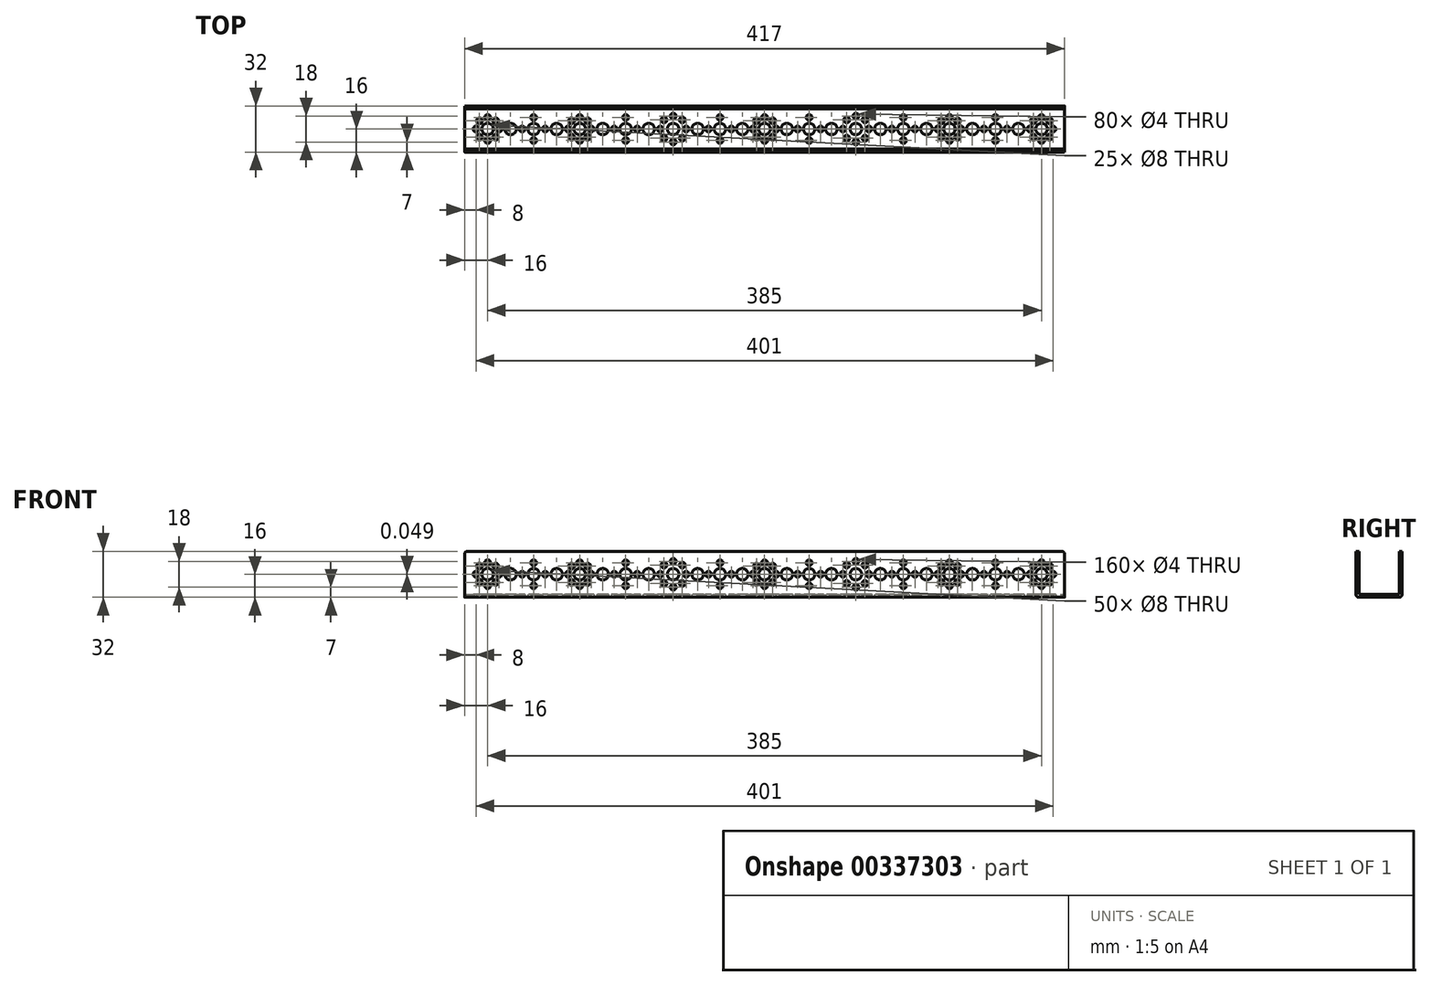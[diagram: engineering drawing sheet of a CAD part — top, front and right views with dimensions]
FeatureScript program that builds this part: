
annotation { "Feature Type Name" : "Feature", "Feature Type Description" : "" }
export const myFeature = defineFeature(function(context is Context, id is Id, definition is map)
    precondition{}
    {
        {
            var Q0;
            Q0=qCreatedBy(makeId("Top.planeOp"),FACE);
            var sketch = newSketch(context, id + "F0", { "sketchPlane" : qUnion([Q0])});
            skLineSegment(sketch, "E0", {"start": v(-32.28, 88.8) * mm, "end": v(-32.28, 86.16) * mm});
            skLineSegment(sketch, "E1", {"start": v(-32.28, 86.16) * mm, "end": v(-32.28, 83.52) * mm});
            skLineSegment(sketch, "E2", {"start": v(-34.35, 86.16) * mm, "end": v(-32.28, 86.16) * mm});
            skLineSegment(sketch, "E3", {"start": v(-30.23, 86.16) * mm, "end": v(-32.28, 86.16) * mm});
            skLineSegment(sketch, "E4", {"start": v(-32.28, 86.16) * mm, "end": v(-30.85, 87.6) * mm});
            skLineSegment(sketch, "E5", {"start": v(-32.28, 86.16) * mm, "end": v(-33.68, 84.77) * mm});
            skLineSegment(sketch, "E6", {"start": v(-32.28, 86.16) * mm, "end": v(-33.68, 87.56) * mm});
            skLineSegment(sketch, "E7", {"start": v(-32.28, 86.16) * mm, "end": v(-30.63, 84.51) * mm});
            skCircle(sketch, "E8", {"center": v(-32.28, 86.16) * mm, "radius": 4 * mm});
            skCircle(sketch, "E9", {"center": v(-38.65, 92.53) * mm, "radius": 2 * mm});
            skCircle(sketch, "E10", {"center": v(-32.28, 95.16) * mm, "radius": 2 * mm});
            skCircle(sketch, "E11", {"center": v(-25.92, 92.53) * mm, "radius": 2 * mm});
            skCircle(sketch, "E12", {"center": v(-23.28, 86.16) * mm, "radius": 2 * mm});
            skCircle(sketch, "E13", {"center": v(-41.28, 86.16) * mm, "radius": 2 * mm});
            skCircle(sketch, "E14", {"center": v(-38.65, 79.8) * mm, "radius": 2 * mm});
            skCircle(sketch, "E15", {"center": v(-32.28, 77.16) * mm, "radius": 2 * mm});
            skCircle(sketch, "E16", {"center": v(-25.92, 79.8) * mm, "radius": 2 * mm});
            skCircle(sketch, "E17", {"center": v(-14.28, 86.16) * mm, "radius": 4 * mm});
            skCircle(sketch, "E18", {"center": v(3.72, 86.16) * mm, "radius": 4 * mm});
            skCircle(sketch, "E19", {"center": v(3.72, 95.16) * mm, "radius": 2 * mm});
            skCircle(sketch, "E20", {"center": v(12.72, 86.16) * mm, "radius": 2 * mm});
            skCircle(sketch, "E21", {"center": v(3.72, 77.16) * mm, "radius": 2 * mm});
            skCircle(sketch, "E22", {"center": v(-5.28, 86.16) * mm, "radius": 2 * mm});
            skCircle(sketch, "E23", {"center": v(21.72, 86.16) * mm, "radius": 4 * mm});
            skLineSegment(sketch, "E24.bottom", {"start": v(208.5, 16) * mm, "end": v(-208.5, 16) * mm});
            skLineSegment(sketch, "E24.top", {"start": v(208.5, -16) * mm, "end": v(-208.5, -16) * mm});
            skLineSegment(sketch, "E24.left", {"start": v(208.5, 16) * mm, "end": v(208.5, -16) * mm});
            skLineSegment(sketch, "E24.right", {"start": v(-208.5, 16) * mm, "end": v(-208.5, -16) * mm});
            skPoint(sketch, "E24.middle", {"position": v(0, 0) * mm});
            skLineSegment(sketch, "E25", {"start": v(-192.5, 2.64) * mm, "end": v(-192.5, 0) * mm});
            skLineSegment(sketch, "E26", {"start": v(-192.5, 0) * mm, "end": v(-192.5, -2.64) * mm});
            skLineSegment(sketch, "E27", {"start": v(-194.35, 0) * mm, "end": v(-192.5, 0) * mm});
            skLineSegment(sketch, "E28", {"start": v(-188.78, 0) * mm, "end": v(-192.5, 0) * mm});
            skLineSegment(sketch, "E29", {"start": v(-192.5, 0) * mm, "end": v(-191.22, 1.28) * mm});
            skLineSegment(sketch, "E30", {"start": v(-192.5, 0) * mm, "end": v(-193.9, -1.4) * mm});
            skLineSegment(sketch, "E31", {"start": v(-192.5, 0) * mm, "end": v(-193.9, 1.4) * mm});
            skLineSegment(sketch, "E32", {"start": v(-192.5, 0) * mm, "end": v(-191.12, -1.38) * mm});
            skCircle(sketch, "E33", {"center": v(-192.5, 0) * mm, "radius": 4 * mm});
            skCircle(sketch, "E34", {"center": v(-198.16, 5.66) * mm, "radius": 2 * mm});
            skCircle(sketch, "E35", {"center": v(-192.5, 8) * mm, "radius": 2 * mm});
            skCircle(sketch, "E36", {"center": v(-186.84, 5.66) * mm, "radius": 2 * mm});
            skCircle(sketch, "E37", {"center": v(-184.5, 0) * mm, "radius": 2 * mm});
            skCircle(sketch, "E38", {"center": v(-200.5, 0) * mm, "radius": 2 * mm});
            skCircle(sketch, "E39", {"center": v(-198.16, -5.66) * mm, "radius": 2 * mm});
            skCircle(sketch, "E40", {"center": v(-192.5, -8) * mm, "radius": 2 * mm});
            skCircle(sketch, "E41", {"center": v(-186.84, -5.66) * mm, "radius": 2 * mm});
            skCircle(sketch, "E42", {"center": v(-176.5, 0) * mm, "radius": 4 * mm});
            skCircle(sketch, "E43", {"center": v(-160.5, 0) * mm, "radius": 4 * mm});
            skCircle(sketch, "E44", {"center": v(-160.5, 8) * mm, "radius": 2 * mm});
            skCircle(sketch, "E45", {"center": v(-152.5, 0) * mm, "radius": 2 * mm});
            skCircle(sketch, "E46", {"center": v(-160.5, -8) * mm, "radius": 2 * mm});
            skCircle(sketch, "E47", {"center": v(-168.5, 0) * mm, "radius": 2 * mm});
            skCircle(sketch, "E48", {"center": v(-144.5, 0) * mm, "radius": 4 * mm});
            skLineSegment(sketch, "E49", {"start": v(-128.5, 2.64) * mm, "end": v(-128.5, 0) * mm});
            skLineSegment(sketch, "E50", {"start": v(-128.5, 0) * mm, "end": v(-128.5, -2.64) * mm});
            skLineSegment(sketch, "E51", {"start": v(-128.5, 0) * mm, "end": v(-121.3, 0) * mm});
            skLineSegment(sketch, "E52", {"start": v(-117.23, 0) * mm, "end": v(-128.5, 0) * mm});
            skLineSegment(sketch, "E53", {"start": v(-128.5, 0) * mm, "end": v(-127.07, 1.43) * mm});
            skLineSegment(sketch, "E54", {"start": v(-128.5, 0) * mm, "end": v(-129.9, -1.4) * mm});
            skLineSegment(sketch, "E55", {"start": v(-128.5, 0) * mm, "end": v(-129.9, 1.4) * mm});
            skLineSegment(sketch, "E56", {"start": v(-128.5, 0) * mm, "end": v(-126.85, -1.65) * mm});
            skCircle(sketch, "E57", {"center": v(-128.5, 0) * mm, "radius": 4 * mm});
            skCircle(sketch, "E58", {"center": v(-134.16, 5.66) * mm, "radius": 2 * mm});
            skCircle(sketch, "E59", {"center": v(-128.5, 8) * mm, "radius": 2 * mm});
            skCircle(sketch, "E60", {"center": v(-122.84, 5.66) * mm, "radius": 2 * mm});
            skCircle(sketch, "E61", {"center": v(-120.5, 0) * mm, "radius": 2 * mm});
            skCircle(sketch, "E62", {"center": v(-136.5, 0) * mm, "radius": 2 * mm});
            skCircle(sketch, "E63", {"center": v(-134.16, -5.66) * mm, "radius": 2 * mm});
            skCircle(sketch, "E64", {"center": v(-128.5, -8) * mm, "radius": 2 * mm});
            skCircle(sketch, "E65", {"center": v(-122.84, -5.66) * mm, "radius": 2 * mm});
            skCircle(sketch, "E66", {"center": v(-112.5, 0) * mm, "radius": 4 * mm});
            skCircle(sketch, "E67", {"center": v(-96.5, 0) * mm, "radius": 4 * mm});
            skCircle(sketch, "E68", {"center": v(-96.5, 8) * mm, "radius": 2 * mm});
            skCircle(sketch, "E69", {"center": v(-88.5, 0) * mm, "radius": 2 * mm});
            skCircle(sketch, "E70", {"center": v(-96.5, -8) * mm, "radius": 2 * mm});
            skCircle(sketch, "E71", {"center": v(-104.5, 0) * mm, "radius": 2 * mm});
            skCircle(sketch, "E72", {"center": v(-80.5, 0) * mm, "radius": 4 * mm});
            skLineSegment(sketch, "E73", {"start": v(-63.5, 2.64) * mm, "end": v(-63.5, 0) * mm});
            skLineSegment(sketch, "E74", {"start": v(-63.5, 0) * mm, "end": v(-63.5, -2.64) * mm});
            skLineSegment(sketch, "E75", {"start": v(-65.6, 0) * mm, "end": v(-63.5, 0) * mm});
            skLineSegment(sketch, "E76", {"start": v(-61.56, 0) * mm, "end": v(-63.5, 0) * mm});
            skLineSegment(sketch, "E77", {"start": v(-63.5, 0) * mm, "end": v(-62.07, 1.43) * mm});
            skLineSegment(sketch, "E78", {"start": v(-63.5, 0) * mm, "end": v(-64.9, -1.4) * mm});
            skLineSegment(sketch, "E79", {"start": v(-63.5, 0) * mm, "end": v(-64.9, 1.4) * mm});
            skLineSegment(sketch, "E80", {"start": v(-63.5, 0) * mm, "end": v(-61.85, -1.65) * mm});
            skCircle(sketch, "E81", {"center": v(-63.5, 0) * mm, "radius": 4 * mm});
            skCircle(sketch, "E82", {"center": v(-69.86, 6.36) * mm, "radius": 2 * mm});
            skCircle(sketch, "E83", {"center": v(-63.5, 9) * mm, "radius": 2 * mm});
            skCircle(sketch, "E84", {"center": v(-57.14, 6.36) * mm, "radius": 2 * mm});
            skCircle(sketch, "E85", {"center": v(-54.5, 0) * mm, "radius": 2 * mm});
            skCircle(sketch, "E86", {"center": v(-72.5, 0) * mm, "radius": 2 * mm});
            skCircle(sketch, "E87", {"center": v(-69.86, -6.36) * mm, "radius": 2 * mm});
            skCircle(sketch, "E88", {"center": v(-63.5, -9) * mm, "radius": 2 * mm});
            skCircle(sketch, "E89", {"center": v(-57.14, -6.36) * mm, "radius": 2 * mm});
            skCircle(sketch, "E90", {"center": v(-46.5, 0) * mm, "radius": 4 * mm});
            skCircle(sketch, "E91", {"center": v(-31, 0) * mm, "radius": 4 * mm});
            skCircle(sketch, "E92", {"center": v(-31, 8) * mm, "radius": 2 * mm});
            skCircle(sketch, "E93", {"center": v(-23, 0) * mm, "radius": 2 * mm});
            skCircle(sketch, "E94", {"center": v(-31, -8) * mm, "radius": 2 * mm});
            skCircle(sketch, "E95", {"center": v(-39, 0) * mm, "radius": 2 * mm});
            skCircle(sketch, "E96", {"center": v(-15.5, 0) * mm, "radius": 4 * mm});
            skCircle(sketch, "E97.MirrorC", {"center": v(192.5, 0) * mm, "radius": 4 * mm});
            skCircle(sketch, "E98.MirrorC", {"center": v(192.5, 8) * mm, "radius": 2 * mm});
            skCircle(sketch, "E99.MirrorC", {"center": v(198.16, 5.66) * mm, "radius": 2 * mm});
            skCircle(sketch, "E100.MirrorC", {"center": v(200.5, 0) * mm, "radius": 2 * mm});
            skCircle(sketch, "E101.MirrorC", {"center": v(198.16, -5.66) * mm, "radius": 2 * mm});
            skCircle(sketch, "E102.MirrorC", {"center": v(192.5, -8) * mm, "radius": 2 * mm});
            skCircle(sketch, "E103.MirrorC", {"center": v(186.84, -5.66) * mm, "radius": 2 * mm});
            skCircle(sketch, "E104.MirrorC", {"center": v(184.5, 0) * mm, "radius": 2 * mm});
            skCircle(sketch, "E105.MirrorC", {"center": v(186.84, 5.66) * mm, "radius": 2 * mm});
            skCircle(sketch, "E106.MirrorC", {"center": v(176.5, 0) * mm, "radius": 4 * mm});
            skCircle(sketch, "E107.MirrorC", {"center": v(168.5, 0) * mm, "radius": 2 * mm});
            skCircle(sketch, "E108.MirrorC", {"center": v(160.5, 0) * mm, "radius": 4 * mm});
            skCircle(sketch, "E109.MirrorC", {"center": v(160.5, 8) * mm, "radius": 2 * mm});
            skCircle(sketch, "E110.MirrorC", {"center": v(160.5, -8) * mm, "radius": 2 * mm});
            skCircle(sketch, "E111.MirrorC", {"center": v(152.5, 0) * mm, "radius": 2 * mm});
            skCircle(sketch, "E112.MirrorC", {"center": v(144.5, 0) * mm, "radius": 4 * mm});
            skCircle(sketch, "E113.MirrorC", {"center": v(136.5, 0) * mm, "radius": 2 * mm});
            skCircle(sketch, "E114.MirrorC", {"center": v(128.5, 0) * mm, "radius": 4 * mm});
            skCircle(sketch, "E115.MirrorC", {"center": v(134.16, 5.66) * mm, "radius": 2 * mm});
            skCircle(sketch, "E116.MirrorC", {"center": v(128.5, 8) * mm, "radius": 2 * mm});
            skCircle(sketch, "E117.MirrorC", {"center": v(134.16, -5.66) * mm, "radius": 2 * mm});
            skCircle(sketch, "E118.MirrorC", {"center": v(128.5, -8) * mm, "radius": 2 * mm});
            skCircle(sketch, "E119.MirrorC", {"center": v(122.84, -5.66) * mm, "radius": 2 * mm});
            skCircle(sketch, "E120.MirrorC", {"center": v(120.5, 0) * mm, "radius": 2 * mm});
            skCircle(sketch, "E121.MirrorC", {"center": v(122.84, 5.66) * mm, "radius": 2 * mm});
            skCircle(sketch, "E122.MirrorC", {"center": v(112.5, 0) * mm, "radius": 4 * mm});
            skCircle(sketch, "E123.MirrorC", {"center": v(104.5, 0) * mm, "radius": 2 * mm});
            skCircle(sketch, "E124.MirrorC", {"center": v(96.5, 8) * mm, "radius": 2 * mm});
            skCircle(sketch, "E125.MirrorC", {"center": v(96.5, 0) * mm, "radius": 4 * mm});
            skCircle(sketch, "E126.MirrorC", {"center": v(96.5, -8) * mm, "radius": 2 * mm});
            skCircle(sketch, "E127.MirrorC", {"center": v(88.5, 0) * mm, "radius": 2 * mm});
            skCircle(sketch, "E128.MirrorC", {"center": v(80.5, 0) * mm, "radius": 4 * mm});
            skCircle(sketch, "E129.MirrorC", {"center": v(72.5, 0) * mm, "radius": 2 * mm});
            skCircle(sketch, "E130.MirrorC", {"center": v(63.5, 0) * mm, "radius": 4 * mm});
            skCircle(sketch, "E131.MirrorC", {"center": v(69.86, -6.36) * mm, "radius": 2 * mm});
            skCircle(sketch, "E132.MirrorC", {"center": v(63.5, -9) * mm, "radius": 2 * mm});
            skCircle(sketch, "E133.MirrorC", {"center": v(69.86, 6.36) * mm, "radius": 2 * mm});
            skCircle(sketch, "E134.MirrorC", {"center": v(63.5, 9) * mm, "radius": 2 * mm});
            skCircle(sketch, "E135.MirrorC", {"center": v(57.14, 6.36) * mm, "radius": 2 * mm});
            skCircle(sketch, "E136.MirrorC", {"center": v(54.5, 0) * mm, "radius": 2 * mm});
            skCircle(sketch, "E137.MirrorC", {"center": v(57.14, -6.36) * mm, "radius": 2 * mm});
            skCircle(sketch, "E138.MirrorC", {"center": v(46.5, 0) * mm, "radius": 4 * mm});
            skLineSegment(sketch, "E139", {"start": v(0, 2.64) * mm, "end": v(0, 0) * mm});
            skLineSegment(sketch, "E140", {"start": v(0, 0) * mm, "end": v(0, -2.64) * mm});
            skLineSegment(sketch, "E141", {"start": v(-2.06, 0) * mm, "end": v(0, 0) * mm});
            skLineSegment(sketch, "E142", {"start": v(2.05, 0) * mm, "end": v(0, 0) * mm});
            skLineSegment(sketch, "E143", {"start": v(0, 0) * mm, "end": v(1.43, 1.43) * mm});
            skLineSegment(sketch, "E144", {"start": v(0, 0) * mm, "end": v(-1.4, -1.4) * mm});
            skLineSegment(sketch, "E145", {"start": v(0, 0) * mm, "end": v(-1.4, 1.4) * mm});
            skLineSegment(sketch, "E146", {"start": v(0, 0) * mm, "end": v(1.65, -1.65) * mm});
            skCircle(sketch, "E147", {"center": v(0, 0) * mm, "radius": 4 * mm});
            skCircle(sketch, "E148", {"center": v(-5.66, 5.66) * mm, "radius": 2 * mm});
            skCircle(sketch, "E149", {"center": v(0, 8) * mm, "radius": 2 * mm});
            skCircle(sketch, "E150", {"center": v(5.66, 5.66) * mm, "radius": 2 * mm});
            skCircle(sketch, "E151", {"center": v(8, 0) * mm, "radius": 2 * mm});
            skCircle(sketch, "E152", {"center": v(-8, 0) * mm, "radius": 2 * mm});
            skCircle(sketch, "E153", {"center": v(-5.66, -5.66) * mm, "radius": 2 * mm});
            skCircle(sketch, "E154", {"center": v(0, -8) * mm, "radius": 2 * mm});
            skCircle(sketch, "E155", {"center": v(5.66, -5.66) * mm, "radius": 2 * mm});
            skCircle(sketch, "E156.MirrorC", {"center": v(15.5, 0) * mm, "radius": 4 * mm});
            skCircle(sketch, "E157.MirrorC", {"center": v(31, 0) * mm, "radius": 4 * mm});
            skCircle(sketch, "E158.MirrorC", {"center": v(23, 0) * mm, "radius": 2 * mm});
            skCircle(sketch, "E159.MirrorC", {"center": v(31, -8) * mm, "radius": 2 * mm});
            skCircle(sketch, "E160.MirrorC", {"center": v(39, 0) * mm, "radius": 2 * mm});
            skCircle(sketch, "E161.MirrorC", {"center": v(31, 8) * mm, "radius": 2 * mm});
            skSolve(sketch);
        }
        {
            var Q0;
            Q0=makeQuery(id+"F0.imprint","IMPRINT",FACE,{"disambiguationData":[TD([[makeQuery(id+"F0.imprint","IMPRINT",EDGE,{"derivedFrom":sQuery(id+"F0.wireOp",EDGE,"E24.bottom")}),1.0]])]});
            extrude(context, id + "F1", {"entities" : qUnion([Q0]), "depth" : 2 * mm});
        }
        {
            var Q0;
            Q0=sQuery(id+"F0.wireOp",EDGE,"E24.top");
            cPlane(context, id + "F2", {"entities" : qUnion([Q0]), "cplaneType" : CPlaneType.LINE_ANGLE, "offset" : 25.4 * mm, "angle" : 0 * degree, "width" : 152.4 * mm, "height" : 152.4 * mm});
        }
        {
            var Q0;
            Q0=sQuery(id+"F0.wireOp",EDGE,"E24.bottom");
            cPlane(context, id + "F3", {"entities" : qUnion([Q0]), "cplaneType" : CPlaneType.LINE_ANGLE, "offset" : 25.4 * mm, "angle" : 0 * degree, "width" : 152.4 * mm, "height" : 152.4 * mm});
        }
        {
            var Q0;
            Q0=qCreatedBy(id+"F2.planeOp",FACE);
            var sketch = newSketch(context, id + "F4", { "sketchPlane" : qUnion([Q0])});
            skLineSegment(sketch, "E162.bottom", {"start": v(208.5, 32) * mm, "end": v(-208.5, 32) * mm});
            skLineSegment(sketch, "E162.top", {"start": v(208.5, 0) * mm, "end": v(-208.5, 0) * mm});
            skLineSegment(sketch, "E162.right", {"start": v(-208.5, 32) * mm, "end": v(-208.5, 0) * mm});
            skPoint(sketch, "E162.middle", {"position": v(0, 16) * mm});
            skLineSegment(sketch, "E163", {"start": v(-192.5, 18.7) * mm, "end": v(-192.5, 16.05) * mm});
            skLineSegment(sketch, "E164", {"start": v(-192.5, 16.05) * mm, "end": v(-192.5, 13.4) * mm});
            skLineSegment(sketch, "E165", {"start": v(-194.35, 16.05) * mm, "end": v(-192.5, 16.05) * mm});
            skLineSegment(sketch, "E166", {"start": v(-188.78, 16.05) * mm, "end": v(-192.5, 16.05) * mm});
            skLineSegment(sketch, "E167", {"start": v(-192.5, 16.05) * mm, "end": v(-191.22, 17.33) * mm});
            skLineSegment(sketch, "E168", {"start": v(-192.5, 16.05) * mm, "end": v(-193.9, 14.65) * mm});
            skLineSegment(sketch, "E169", {"start": v(-192.5, 16.05) * mm, "end": v(-193.9, 17.44) * mm});
            skLineSegment(sketch, "E170", {"start": v(-192.5, 16.05) * mm, "end": v(-191.12, 14.67) * mm});
            skCircle(sketch, "E171", {"center": v(-192.5, 16.05) * mm, "radius": 4 * mm});
            skCircle(sketch, "E172", {"center": v(-198.16, 21.7) * mm, "radius": 2 * mm});
            skCircle(sketch, "E173", {"center": v(-192.5, 24.05) * mm, "radius": 2 * mm});
            skCircle(sketch, "E174", {"center": v(-186.84, 21.7) * mm, "radius": 2 * mm});
            skCircle(sketch, "E175", {"center": v(-184.5, 16.05) * mm, "radius": 2 * mm});
            skCircle(sketch, "E176", {"center": v(-200.5, 16.05) * mm, "radius": 2 * mm});
            skCircle(sketch, "E177", {"center": v(-198.16, 10.4) * mm, "radius": 2 * mm});
            skCircle(sketch, "E178", {"center": v(-192.5, 8.05) * mm, "radius": 2 * mm});
            skCircle(sketch, "E179", {"center": v(-186.84, 10.4) * mm, "radius": 2 * mm});
            skCircle(sketch, "E180", {"center": v(-176.5, 16) * mm, "radius": 4 * mm});
            skCircle(sketch, "E181", {"center": v(-160.5, 16) * mm, "radius": 4 * mm});
            skCircle(sketch, "E182", {"center": v(-160.5, 24) * mm, "radius": 2 * mm});
            skCircle(sketch, "E183", {"center": v(-152.5, 16) * mm, "radius": 2 * mm});
            skCircle(sketch, "E184", {"center": v(-160.5, 8) * mm, "radius": 2 * mm});
            skCircle(sketch, "E185", {"center": v(-168.5, 16) * mm, "radius": 2 * mm});
            skCircle(sketch, "E186", {"center": v(-144.5, 16) * mm, "radius": 4 * mm});
            skLineSegment(sketch, "E187", {"start": v(-128.5, 18.64) * mm, "end": v(-128.5, 16) * mm});
            skLineSegment(sketch, "E188", {"start": v(-128.5, 16) * mm, "end": v(-128.5, 13.36) * mm});
            skLineSegment(sketch, "E189", {"start": v(-128.5, 16) * mm, "end": v(-121.3, 16) * mm});
            skLineSegment(sketch, "E190", {"start": v(-117.23, 16) * mm, "end": v(-128.5, 16) * mm});
            skLineSegment(sketch, "E191", {"start": v(-128.5, 16) * mm, "end": v(-127.07, 17.43) * mm});
            skLineSegment(sketch, "E192", {"start": v(-128.5, 16) * mm, "end": v(-129.9, 14.6) * mm});
            skLineSegment(sketch, "E193", {"start": v(-128.5, 16) * mm, "end": v(-129.9, 17.4) * mm});
            skLineSegment(sketch, "E194", {"start": v(-128.5, 16) * mm, "end": v(-126.85, 14.35) * mm});
            skCircle(sketch, "E195", {"center": v(-128.5, 16) * mm, "radius": 4 * mm});
            skCircle(sketch, "E196", {"center": v(-134.16, 21.66) * mm, "radius": 2 * mm});
            skCircle(sketch, "E197", {"center": v(-128.5, 24) * mm, "radius": 2 * mm});
            skCircle(sketch, "E198", {"center": v(-122.84, 21.66) * mm, "radius": 2 * mm});
            skCircle(sketch, "E199", {"center": v(-120.5, 16) * mm, "radius": 2 * mm});
            skCircle(sketch, "E200", {"center": v(-136.5, 16) * mm, "radius": 2 * mm});
            skCircle(sketch, "E201", {"center": v(-134.16, 10.34) * mm, "radius": 2 * mm});
            skCircle(sketch, "E202", {"center": v(-128.5, 8) * mm, "radius": 2 * mm});
            skCircle(sketch, "E203", {"center": v(-122.84, 10.34) * mm, "radius": 2 * mm});
            skCircle(sketch, "E204", {"center": v(-112.5, 16) * mm, "radius": 4 * mm});
            skCircle(sketch, "E205", {"center": v(-96.5, 16) * mm, "radius": 4 * mm});
            skCircle(sketch, "E206", {"center": v(-96.5, 24) * mm, "radius": 2 * mm});
            skCircle(sketch, "E207", {"center": v(-88.5, 16) * mm, "radius": 2 * mm});
            skCircle(sketch, "E208", {"center": v(-96.5, 8) * mm, "radius": 2 * mm});
            skCircle(sketch, "E209", {"center": v(-104.5, 16) * mm, "radius": 2 * mm});
            skCircle(sketch, "E210", {"center": v(-80.5, 16) * mm, "radius": 4 * mm});
            skLineSegment(sketch, "E211", {"start": v(-63.5, 18.64) * mm, "end": v(-63.5, 16) * mm});
            skLineSegment(sketch, "E212", {"start": v(-63.5, 16) * mm, "end": v(-63.5, 13.36) * mm});
            skLineSegment(sketch, "E213", {"start": v(-65.6, 16) * mm, "end": v(-63.5, 16) * mm});
            skLineSegment(sketch, "E214", {"start": v(-61.56, 16) * mm, "end": v(-63.5, 16) * mm});
            skLineSegment(sketch, "E215", {"start": v(-63.5, 16) * mm, "end": v(-62.07, 17.43) * mm});
            skLineSegment(sketch, "E216", {"start": v(-63.5, 16) * mm, "end": v(-64.9, 14.6) * mm});
            skLineSegment(sketch, "E217", {"start": v(-63.5, 16) * mm, "end": v(-64.9, 17.4) * mm});
            skLineSegment(sketch, "E218", {"start": v(-63.5, 16) * mm, "end": v(-61.85, 14.35) * mm});
            skCircle(sketch, "E219", {"center": v(-63.5, 16) * mm, "radius": 4 * mm});
            skCircle(sketch, "E220", {"center": v(-69.86, 22.36) * mm, "radius": 2 * mm});
            skCircle(sketch, "E221", {"center": v(-63.5, 25) * mm, "radius": 2 * mm});
            skCircle(sketch, "E222", {"center": v(-57.14, 22.36) * mm, "radius": 2 * mm});
            skCircle(sketch, "E223", {"center": v(-54.5, 16) * mm, "radius": 2 * mm});
            skCircle(sketch, "E224", {"center": v(-72.5, 16) * mm, "radius": 2 * mm});
            skCircle(sketch, "E225", {"center": v(-69.86, 9.64) * mm, "radius": 2 * mm});
            skCircle(sketch, "E226", {"center": v(-63.5, 7) * mm, "radius": 2 * mm});
            skCircle(sketch, "E227", {"center": v(-57.14, 9.64) * mm, "radius": 2 * mm});
            skCircle(sketch, "E228", {"center": v(-46.5, 16) * mm, "radius": 4 * mm});
            skCircle(sketch, "E229", {"center": v(-31, 16) * mm, "radius": 4 * mm});
            skCircle(sketch, "E230", {"center": v(-31, 24) * mm, "radius": 2 * mm});
            skCircle(sketch, "E231", {"center": v(-23, 16) * mm, "radius": 2 * mm});
            skCircle(sketch, "E232", {"center": v(-31, 8) * mm, "radius": 2 * mm});
            skCircle(sketch, "E233", {"center": v(-39, 16) * mm, "radius": 2 * mm});
            skCircle(sketch, "E234", {"center": v(-15.5, 16) * mm, "radius": 4 * mm});
            skLineSegment(sketch, "E235", {"start": v(0, 18.64) * mm, "end": v(0, 16) * mm});
            skLineSegment(sketch, "E236", {"start": v(0, 16) * mm, "end": v(0, 13.36) * mm});
            skLineSegment(sketch, "E237", {"start": v(-2.06, 16) * mm, "end": v(0, 16) * mm});
            skLineSegment(sketch, "E238", {"start": v(2.05, 16) * mm, "end": v(0, 16) * mm});
            skLineSegment(sketch, "E239", {"start": v(0, 16) * mm, "end": v(1.43, 17.43) * mm});
            skLineSegment(sketch, "E240", {"start": v(0, 16) * mm, "end": v(-1.4, 14.6) * mm});
            skLineSegment(sketch, "E241", {"start": v(0, 16) * mm, "end": v(-1.4, 17.4) * mm});
            skLineSegment(sketch, "E242", {"start": v(0, 16) * mm, "end": v(1.65, 14.35) * mm});
            skCircle(sketch, "E243", {"center": v(0, 16) * mm, "radius": 4 * mm});
            skCircle(sketch, "E244", {"center": v(-5.66, 21.66) * mm, "radius": 2 * mm});
            skCircle(sketch, "E245", {"center": v(0, 24) * mm, "radius": 2 * mm});
            skCircle(sketch, "E246", {"center": v(5.66, 21.66) * mm, "radius": 2 * mm});
            skCircle(sketch, "E247", {"center": v(8, 16) * mm, "radius": 2 * mm});
            skCircle(sketch, "E248", {"center": v(-8, 16) * mm, "radius": 2 * mm});
            skCircle(sketch, "E249", {"center": v(-5.66, 10.34) * mm, "radius": 2 * mm});
            skCircle(sketch, "E250", {"center": v(0, 8) * mm, "radius": 2 * mm});
            skCircle(sketch, "E251", {"center": v(5.66, 10.34) * mm, "radius": 2 * mm});
            skLineSegment(sketch, "E252", {"start": v(208.5, 0) * mm, "end": v(208.5, 32) * mm});
            skPoint(sketch, "E253", {"position": v(-208.5, 16) * mm});
            skCircle(sketch, "E254.MirrorC", {"center": v(200.5, 16.05) * mm, "radius": 2 * mm});
            skCircle(sketch, "E255.MirrorC", {"center": v(198.16, 21.7) * mm, "radius": 2 * mm});
            skCircle(sketch, "E256.MirrorC", {"center": v(192.5, 24.05) * mm, "radius": 2 * mm});
            skCircle(sketch, "E257.MirrorC", {"center": v(186.84, 21.7) * mm, "radius": 2 * mm});
            skCircle(sketch, "E258.MirrorC", {"center": v(184.5, 16.05) * mm, "radius": 2 * mm});
            skCircle(sketch, "E259.MirrorC", {"center": v(186.84, 10.4) * mm, "radius": 2 * mm});
            skCircle(sketch, "E260.MirrorC", {"center": v(192.5, 8.05) * mm, "radius": 2 * mm});
            skCircle(sketch, "E261.MirrorC", {"center": v(198.16, 10.4) * mm, "radius": 2 * mm});
            skCircle(sketch, "E262.MirrorC", {"center": v(192.5, 16.05) * mm, "radius": 4 * mm});
            skCircle(sketch, "E263.MirrorC", {"center": v(176.5, 16) * mm, "radius": 4 * mm});
            skCircle(sketch, "E264.MirrorC", {"center": v(168.5, 16) * mm, "radius": 2 * mm});
            skCircle(sketch, "E265.MirrorC", {"center": v(160.5, 24) * mm, "radius": 2 * mm});
            skCircle(sketch, "E266.MirrorC", {"center": v(152.5, 16) * mm, "radius": 2 * mm});
            skCircle(sketch, "E267.MirrorC", {"center": v(160.5, 8) * mm, "radius": 2 * mm});
            skCircle(sketch, "E268.MirrorC", {"center": v(160.5, 16) * mm, "radius": 4 * mm});
            skCircle(sketch, "E269.MirrorC", {"center": v(144.5, 16) * mm, "radius": 4 * mm});
            skCircle(sketch, "E270.MirrorC", {"center": v(136.5, 16) * mm, "radius": 2 * mm});
            skCircle(sketch, "E271.MirrorC", {"center": v(134.16, 21.66) * mm, "radius": 2 * mm});
            skCircle(sketch, "E272.MirrorC", {"center": v(128.5, 24) * mm, "radius": 2 * mm});
            skCircle(sketch, "E273.MirrorC", {"center": v(122.84, 21.66) * mm, "radius": 2 * mm});
            skCircle(sketch, "E274.MirrorC", {"center": v(120.5, 16) * mm, "radius": 2 * mm});
            skCircle(sketch, "E275.MirrorC", {"center": v(122.84, 10.34) * mm, "radius": 2 * mm});
            skCircle(sketch, "E276.MirrorC", {"center": v(128.5, 8) * mm, "radius": 2 * mm});
            skCircle(sketch, "E277.MirrorC", {"center": v(134.16, 10.34) * mm, "radius": 2 * mm});
            skCircle(sketch, "E278.MirrorC", {"center": v(128.5, 16) * mm, "radius": 4 * mm});
            skCircle(sketch, "E279.MirrorC", {"center": v(112.5, 16) * mm, "radius": 4 * mm});
            skCircle(sketch, "E280.MirrorC", {"center": v(104.5, 16) * mm, "radius": 2 * mm});
            skCircle(sketch, "E281.MirrorC", {"center": v(96.5, 24) * mm, "radius": 2 * mm});
            skCircle(sketch, "E282.MirrorC", {"center": v(88.5, 16) * mm, "radius": 2 * mm});
            skCircle(sketch, "E283.MirrorC", {"center": v(96.5, 8) * mm, "radius": 2 * mm});
            skCircle(sketch, "E284.MirrorC", {"center": v(96.5, 16) * mm, "radius": 4 * mm});
            skCircle(sketch, "E285.MirrorC", {"center": v(80.5, 16) * mm, "radius": 4 * mm});
            skCircle(sketch, "E286.MirrorC", {"center": v(72.5, 16) * mm, "radius": 2 * mm});
            skCircle(sketch, "E287.MirrorC", {"center": v(69.86, 22.36) * mm, "radius": 2 * mm});
            skCircle(sketch, "E288.MirrorC", {"center": v(63.5, 25) * mm, "radius": 2 * mm});
            skCircle(sketch, "E289.MirrorC", {"center": v(57.14, 22.36) * mm, "radius": 2 * mm});
            skCircle(sketch, "E290.MirrorC", {"center": v(54.5, 16) * mm, "radius": 2 * mm});
            skCircle(sketch, "E291.MirrorC", {"center": v(57.14, 9.64) * mm, "radius": 2 * mm});
            skCircle(sketch, "E292.MirrorC", {"center": v(63.5, 7) * mm, "radius": 2 * mm});
            skCircle(sketch, "E293.MirrorC", {"center": v(69.86, 9.64) * mm, "radius": 2 * mm});
            skCircle(sketch, "E294.MirrorC", {"center": v(63.5, 16) * mm, "radius": 4 * mm});
            skCircle(sketch, "E295.MirrorC", {"center": v(46.5, 16) * mm, "radius": 4 * mm});
            skCircle(sketch, "E296.MirrorC", {"center": v(39, 16) * mm, "radius": 2 * mm});
            skCircle(sketch, "E297.MirrorC", {"center": v(31, 24) * mm, "radius": 2 * mm});
            skCircle(sketch, "E298.MirrorC", {"center": v(23, 16) * mm, "radius": 2 * mm});
            skCircle(sketch, "E299.MirrorC", {"center": v(31, 8) * mm, "radius": 2 * mm});
            skCircle(sketch, "E300.MirrorC", {"center": v(31, 16) * mm, "radius": 4 * mm});
            skCircle(sketch, "E301.MirrorC", {"center": v(15.5, 16) * mm, "radius": 4 * mm});
            skSolve(sketch);
        }
        {
            var Q0;
            Q0=qCreatedBy(id+"F3.planeOp",FACE);
            var sketch = newSketch(context, id + "F5", { "sketchPlane" : qUnion([Q0])});
            skLineSegment(sketch, "E302.bottom", {"start": v(208.5, 32) * mm, "end": v(-208.5, 32) * mm});
            skLineSegment(sketch, "E302.top", {"start": v(208.5, 0) * mm, "end": v(-208.5, 0) * mm});
            skLineSegment(sketch, "E302.right", {"start": v(-208.5, 32) * mm, "end": v(-208.5, 0) * mm});
            skPoint(sketch, "E302.middle", {"position": v(0, 16) * mm});
            skLineSegment(sketch, "E303", {"start": v(-192.5, 18.7) * mm, "end": v(-192.5, 16.05) * mm});
            skLineSegment(sketch, "E304", {"start": v(-192.5, 16.05) * mm, "end": v(-192.5, 13.4) * mm});
            skLineSegment(sketch, "E305", {"start": v(-194.35, 16.05) * mm, "end": v(-192.5, 16.05) * mm});
            skLineSegment(sketch, "E306", {"start": v(-188.78, 16.05) * mm, "end": v(-192.5, 16.05) * mm});
            skLineSegment(sketch, "E307", {"start": v(-192.5, 16.05) * mm, "end": v(-191.22, 17.33) * mm});
            skLineSegment(sketch, "E308", {"start": v(-192.5, 16.05) * mm, "end": v(-193.9, 14.65) * mm});
            skLineSegment(sketch, "E309", {"start": v(-192.5, 16.05) * mm, "end": v(-193.9, 17.44) * mm});
            skLineSegment(sketch, "E310", {"start": v(-192.5, 16.05) * mm, "end": v(-191.12, 14.67) * mm});
            skCircle(sketch, "E311", {"center": v(-192.5, 16.05) * mm, "radius": 4 * mm});
            skCircle(sketch, "E312", {"center": v(-198.16, 21.7) * mm, "radius": 2 * mm});
            skCircle(sketch, "E313", {"center": v(-192.5, 24.05) * mm, "radius": 2 * mm});
            skCircle(sketch, "E314", {"center": v(-186.84, 21.7) * mm, "radius": 2 * mm});
            skCircle(sketch, "E315", {"center": v(-184.5, 16.05) * mm, "radius": 2 * mm});
            skCircle(sketch, "E316", {"center": v(-200.5, 16.05) * mm, "radius": 2 * mm});
            skCircle(sketch, "E317", {"center": v(-198.16, 10.4) * mm, "radius": 2 * mm});
            skCircle(sketch, "E318", {"center": v(-192.5, 8.05) * mm, "radius": 2 * mm});
            skCircle(sketch, "E319", {"center": v(-186.84, 10.4) * mm, "radius": 2 * mm});
            skCircle(sketch, "E320", {"center": v(-176.5, 16) * mm, "radius": 4 * mm});
            skCircle(sketch, "E321", {"center": v(-160.5, 16) * mm, "radius": 4 * mm});
            skCircle(sketch, "E322", {"center": v(-160.5, 24) * mm, "radius": 2 * mm});
            skCircle(sketch, "E323", {"center": v(-152.5, 16) * mm, "radius": 2 * mm});
            skCircle(sketch, "E324", {"center": v(-160.5, 8) * mm, "radius": 2 * mm});
            skCircle(sketch, "E325", {"center": v(-168.5, 16) * mm, "radius": 2 * mm});
            skCircle(sketch, "E326", {"center": v(-144.5, 16) * mm, "radius": 4 * mm});
            skLineSegment(sketch, "E327", {"start": v(-128.5, 18.64) * mm, "end": v(-128.5, 16) * mm});
            skLineSegment(sketch, "E328", {"start": v(-128.5, 16) * mm, "end": v(-128.5, 13.36) * mm});
            skLineSegment(sketch, "E329", {"start": v(-128.5, 16) * mm, "end": v(-121.3, 16) * mm});
            skLineSegment(sketch, "E330", {"start": v(-117.23, 16) * mm, "end": v(-128.5, 16) * mm});
            skLineSegment(sketch, "E331", {"start": v(-128.5, 16) * mm, "end": v(-127.07, 17.43) * mm});
            skLineSegment(sketch, "E332", {"start": v(-128.5, 16) * mm, "end": v(-129.9, 14.6) * mm});
            skLineSegment(sketch, "E333", {"start": v(-128.5, 16) * mm, "end": v(-129.9, 17.4) * mm});
            skLineSegment(sketch, "E334", {"start": v(-128.5, 16) * mm, "end": v(-126.85, 14.35) * mm});
            skCircle(sketch, "E335", {"center": v(-128.5, 16) * mm, "radius": 4 * mm});
            skCircle(sketch, "E336", {"center": v(-134.16, 21.66) * mm, "radius": 2 * mm});
            skCircle(sketch, "E337", {"center": v(-128.5, 24) * mm, "radius": 2 * mm});
            skCircle(sketch, "E338", {"center": v(-122.84, 21.66) * mm, "radius": 2 * mm});
            skCircle(sketch, "E339", {"center": v(-120.5, 16) * mm, "radius": 2 * mm});
            skCircle(sketch, "E340", {"center": v(-136.5, 16) * mm, "radius": 2 * mm});
            skCircle(sketch, "E341", {"center": v(-134.16, 10.34) * mm, "radius": 2 * mm});
            skCircle(sketch, "E342", {"center": v(-128.5, 8) * mm, "radius": 2 * mm});
            skCircle(sketch, "E343", {"center": v(-122.84, 10.34) * mm, "radius": 2 * mm});
            skCircle(sketch, "E344", {"center": v(-112.5, 16) * mm, "radius": 4 * mm});
            skCircle(sketch, "E345", {"center": v(-96.5, 16) * mm, "radius": 4 * mm});
            skCircle(sketch, "E346", {"center": v(-96.5, 24) * mm, "radius": 2 * mm});
            skCircle(sketch, "E347", {"center": v(-88.5, 16) * mm, "radius": 2 * mm});
            skCircle(sketch, "E348", {"center": v(-96.5, 8) * mm, "radius": 2 * mm});
            skCircle(sketch, "E349", {"center": v(-104.5, 16) * mm, "radius": 2 * mm});
            skCircle(sketch, "E350", {"center": v(-80.5, 16) * mm, "radius": 4 * mm});
            skLineSegment(sketch, "E351", {"start": v(-63.5, 18.64) * mm, "end": v(-63.5, 16) * mm});
            skLineSegment(sketch, "E352", {"start": v(-63.5, 16) * mm, "end": v(-63.5, 13.36) * mm});
            skLineSegment(sketch, "E353", {"start": v(-65.6, 16) * mm, "end": v(-63.5, 16) * mm});
            skLineSegment(sketch, "E354", {"start": v(-61.56, 16) * mm, "end": v(-63.5, 16) * mm});
            skLineSegment(sketch, "E355", {"start": v(-63.5, 16) * mm, "end": v(-62.07, 17.43) * mm});
            skLineSegment(sketch, "E356", {"start": v(-63.5, 16) * mm, "end": v(-64.9, 14.6) * mm});
            skLineSegment(sketch, "E357", {"start": v(-63.5, 16) * mm, "end": v(-64.9, 17.4) * mm});
            skLineSegment(sketch, "E358", {"start": v(-63.5, 16) * mm, "end": v(-61.85, 14.35) * mm});
            skCircle(sketch, "E359", {"center": v(-63.5, 16) * mm, "radius": 4 * mm});
            skCircle(sketch, "E360", {"center": v(-69.86, 22.36) * mm, "radius": 2 * mm});
            skCircle(sketch, "E361", {"center": v(-63.5, 25) * mm, "radius": 2 * mm});
            skCircle(sketch, "E362", {"center": v(-57.14, 22.36) * mm, "radius": 2 * mm});
            skCircle(sketch, "E363", {"center": v(-54.5, 16) * mm, "radius": 2 * mm});
            skCircle(sketch, "E364", {"center": v(-72.5, 16) * mm, "radius": 2 * mm});
            skCircle(sketch, "E365", {"center": v(-69.86, 9.64) * mm, "radius": 2 * mm});
            skCircle(sketch, "E366", {"center": v(-63.5, 7) * mm, "radius": 2 * mm});
            skCircle(sketch, "E367", {"center": v(-57.14, 9.64) * mm, "radius": 2 * mm});
            skCircle(sketch, "E368", {"center": v(-46.5, 16) * mm, "radius": 4 * mm});
            skCircle(sketch, "E369", {"center": v(-31, 16) * mm, "radius": 4 * mm});
            skCircle(sketch, "E370", {"center": v(-31, 24) * mm, "radius": 2 * mm});
            skCircle(sketch, "E371", {"center": v(-23, 16) * mm, "radius": 2 * mm});
            skCircle(sketch, "E372", {"center": v(-31, 8) * mm, "radius": 2 * mm});
            skCircle(sketch, "E373", {"center": v(-39, 16) * mm, "radius": 2 * mm});
            skCircle(sketch, "E374", {"center": v(-15.5, 16) * mm, "radius": 4 * mm});
            skLineSegment(sketch, "E375", {"start": v(0, 18.64) * mm, "end": v(0, 16) * mm});
            skLineSegment(sketch, "E376", {"start": v(0, 16) * mm, "end": v(0, 13.36) * mm});
            skLineSegment(sketch, "E377", {"start": v(-2.06, 16) * mm, "end": v(0, 16) * mm});
            skLineSegment(sketch, "E378", {"start": v(2.05, 16) * mm, "end": v(0, 16) * mm});
            skLineSegment(sketch, "E379", {"start": v(0, 16) * mm, "end": v(1.43, 17.43) * mm});
            skLineSegment(sketch, "E380", {"start": v(0, 16) * mm, "end": v(-1.4, 14.6) * mm});
            skLineSegment(sketch, "E381", {"start": v(0, 16) * mm, "end": v(-1.4, 17.4) * mm});
            skLineSegment(sketch, "E382", {"start": v(0, 16) * mm, "end": v(1.65, 14.35) * mm});
            skCircle(sketch, "E383", {"center": v(0, 16) * mm, "radius": 4 * mm});
            skCircle(sketch, "E384", {"center": v(-5.66, 21.66) * mm, "radius": 2 * mm});
            skCircle(sketch, "E385", {"center": v(0, 24) * mm, "radius": 2 * mm});
            skCircle(sketch, "E386", {"center": v(5.66, 21.66) * mm, "radius": 2 * mm});
            skCircle(sketch, "E387", {"center": v(8, 16) * mm, "radius": 2 * mm});
            skCircle(sketch, "E388", {"center": v(-8, 16) * mm, "radius": 2 * mm});
            skCircle(sketch, "E389", {"center": v(-5.66, 10.34) * mm, "radius": 2 * mm});
            skCircle(sketch, "E390", {"center": v(0, 8) * mm, "radius": 2 * mm});
            skCircle(sketch, "E391", {"center": v(5.66, 10.34) * mm, "radius": 2 * mm});
            skLineSegment(sketch, "E392", {"start": v(208.5, 0) * mm, "end": v(208.5, 32) * mm});
            skPoint(sketch, "E393", {"position": v(-208.5, 16) * mm});
            skCircle(sketch, "E394.MirrorC", {"center": v(15.5, 16) * mm, "radius": 4 * mm});
            skCircle(sketch, "E395.MirrorC", {"center": v(31, 16) * mm, "radius": 4 * mm});
            skCircle(sketch, "E396.MirrorC", {"center": v(23, 16) * mm, "radius": 2 * mm});
            skCircle(sketch, "E397.MirrorC", {"center": v(31, 24) * mm, "radius": 2 * mm});
            skCircle(sketch, "E398.MirrorC", {"center": v(39, 16) * mm, "radius": 2 * mm});
            skCircle(sketch, "E399.MirrorC", {"center": v(31, 8) * mm, "radius": 2 * mm});
            skCircle(sketch, "E400.MirrorC", {"center": v(46.5, 16) * mm, "radius": 4 * mm});
            skCircle(sketch, "E401.MirrorC", {"center": v(63.5, 16) * mm, "radius": 4 * mm});
            skCircle(sketch, "E402.MirrorC", {"center": v(63.5, 25) * mm, "radius": 2 * mm});
            skCircle(sketch, "E403.MirrorC", {"center": v(57.14, 22.36) * mm, "radius": 2 * mm});
            skCircle(sketch, "E404.MirrorC", {"center": v(54.5, 16) * mm, "radius": 2 * mm});
            skCircle(sketch, "E405.MirrorC", {"center": v(57.14, 9.64) * mm, "radius": 2 * mm});
            skCircle(sketch, "E406.MirrorC", {"center": v(63.5, 7) * mm, "radius": 2 * mm});
            skCircle(sketch, "E407.MirrorC", {"center": v(69.86, 9.64) * mm, "radius": 2 * mm});
            skCircle(sketch, "E408.MirrorC", {"center": v(72.5, 16) * mm, "radius": 2 * mm});
            skCircle(sketch, "E409.MirrorC", {"center": v(69.86, 22.36) * mm, "radius": 2 * mm});
            skCircle(sketch, "E410.MirrorC", {"center": v(80.5, 16) * mm, "radius": 4 * mm});
            skCircle(sketch, "E411.MirrorC", {"center": v(88.5, 16) * mm, "radius": 2 * mm});
            skCircle(sketch, "E412.MirrorC", {"center": v(96.5, 16) * mm, "radius": 4 * mm});
            skCircle(sketch, "E413.MirrorC", {"center": v(96.5, 24) * mm, "radius": 2 * mm});
            skCircle(sketch, "E414.MirrorC", {"center": v(104.5, 16) * mm, "radius": 2 * mm});
            skCircle(sketch, "E415.MirrorC", {"center": v(96.5, 8) * mm, "radius": 2 * mm});
            skCircle(sketch, "E416.MirrorC", {"center": v(112.5, 16) * mm, "radius": 4 * mm});
            skCircle(sketch, "E417.MirrorC", {"center": v(120.5, 16) * mm, "radius": 2 * mm});
            skCircle(sketch, "E418.MirrorC", {"center": v(122.84, 10.34) * mm, "radius": 2 * mm});
            skCircle(sketch, "E419.MirrorC", {"center": v(128.5, 8) * mm, "radius": 2 * mm});
            skCircle(sketch, "E420.MirrorC", {"center": v(134.16, 10.34) * mm, "radius": 2 * mm});
            skCircle(sketch, "E421.MirrorC", {"center": v(134.16, 21.66) * mm, "radius": 2 * mm});
            skCircle(sketch, "E422.MirrorC", {"center": v(144.5, 16) * mm, "radius": 4 * mm});
            skCircle(sketch, "E423.MirrorC", {"center": v(152.5, 16) * mm, "radius": 2 * mm});
            skCircle(sketch, "E424.MirrorC", {"center": v(160.5, 16) * mm, "radius": 4 * mm});
            skCircle(sketch, "E425.MirrorC", {"center": v(160.5, 24) * mm, "radius": 2 * mm});
            skCircle(sketch, "E426.MirrorC", {"center": v(168.5, 16) * mm, "radius": 2 * mm});
            skCircle(sketch, "E427.MirrorC", {"center": v(160.5, 8) * mm, "radius": 2 * mm});
            skCircle(sketch, "E428.MirrorC", {"center": v(176.5, 16) * mm, "radius": 4 * mm});
            skCircle(sketch, "E429.MirrorC", {"center": v(192.5, 16.05) * mm, "radius": 4 * mm});
            skCircle(sketch, "E430.MirrorC", {"center": v(192.5, 24.05) * mm, "radius": 2 * mm});
            skCircle(sketch, "E431.MirrorC", {"center": v(198.16, 21.7) * mm, "radius": 2 * mm});
            skCircle(sketch, "E432.MirrorC", {"center": v(200.5, 16.05) * mm, "radius": 2 * mm});
            skCircle(sketch, "E433.MirrorC", {"center": v(198.16, 10.4) * mm, "radius": 2 * mm});
            skCircle(sketch, "E434.MirrorC", {"center": v(192.5, 8.05) * mm, "radius": 2 * mm});
            skCircle(sketch, "E435.MirrorC", {"center": v(186.84, 10.4) * mm, "radius": 2 * mm});
            skCircle(sketch, "E436.MirrorC", {"center": v(128.5, 16) * mm, "radius": 4 * mm});
            skCircle(sketch, "E437.MirrorC", {"center": v(122.84, 21.66) * mm, "radius": 2 * mm});
            skCircle(sketch, "E438.MirrorC", {"center": v(128.5, 24) * mm, "radius": 2 * mm});
            skCircle(sketch, "E439.MirrorC", {"center": v(136.5, 16) * mm, "radius": 2 * mm});
            skCircle(sketch, "E440.MirrorC", {"center": v(184.5, 16.05) * mm, "radius": 2 * mm});
            skCircle(sketch, "E441.MirrorC", {"center": v(186.84, 21.7) * mm, "radius": 2 * mm});
            skSolve(sketch);
        }
        {
            var Q0;
            Q0=makeQuery(id+"F5.imprint","IMPRINT",FACE,{"disambiguationData":[TD([[makeQuery(id+"F5.imprint","IMPRINT",EDGE,{"derivedFrom":sQuery(id+"F5.wireOp",EDGE,"E302.bottom")}),1.0]])]});
            extrude(context, id + "F6", {"entities" : qUnion([Q0]), "operationType" : NewBodyOperationType.ADD, "depth" : 2 * mm});
        }
        {
            var Q0;
            Q0=makeQuery(id+"F4.imprint","IMPRINT",FACE,{"disambiguationData":[TD([[makeQuery(id+"F4.imprint","IMPRINT",EDGE,{"derivedFrom":sQuery(id+"F4.wireOp",EDGE,"E162.bottom")}),1.0]])]});
            extrude(context, id + "F7", {"entities" : qUnion([Q0]), "operationType" : NewBodyOperationType.ADD, "oppositeDirection" : true, "depth" : 2 * mm});
        }
        {
            var Q0;
            Q0=makeQuery(id+"F1.opExtrude","CAP_EDGE",EDGE,{"disambiguationData":[OSD([sQuery(id+"F0.wireOp",EDGE,"E24.top")])],"isStart":true});
            var Q1;
            Q1=makeQuery(id+"F1.opExtrude","CAP_EDGE",EDGE,{"disambiguationData":[OSD([sQuery(id+"F0.wireOp",EDGE,"E24.bottom")])],"isStart":true});
            var Q2;
            Q2=makeQuery(id+"F7.opExtrude","SWEPT_EDGE",EDGE,{"disambiguationData":[OSD([sQuery(id+"F4.wireOp",EDGE,"E162.bottom"),sQuery(id+"F4.wireOp",EDGE,"E252")])]});
            var Q3;
            Q3=makeQuery(id+"F6.opExtrude","SWEPT_EDGE",EDGE,{"disambiguationData":[OSD([sQuery(id+"F5.wireOp",EDGE,"E302.bottom"),sQuery(id+"F5.wireOp",EDGE,"E392")])]});
            var Q4;
            Q4=makeQuery(id+"F6.opExtrude","SWEPT_EDGE",EDGE,{"disambiguationData":[OSD([sQuery(id+"F5.wireOp",EDGE,"E302.bottom"),sQuery(id+"F5.wireOp",EDGE,"E302.right")])]});
            var Q5;
            Q5=makeQuery(id+"F7.opExtrude","SWEPT_EDGE",EDGE,{"disambiguationData":[OSD([sQuery(id+"F4.wireOp",EDGE,"E162.bottom"),sQuery(id+"F4.wireOp",EDGE,"E162.right")])]});
            fillet(context, id + "F8", {"entities" : qUnion([Q0, Q1, Q2, Q3, Q4, Q5]), "radius" : 2 * mm, "tangentPropagation" : true, "allowEdgeOverflow" : false});
        }
    });
